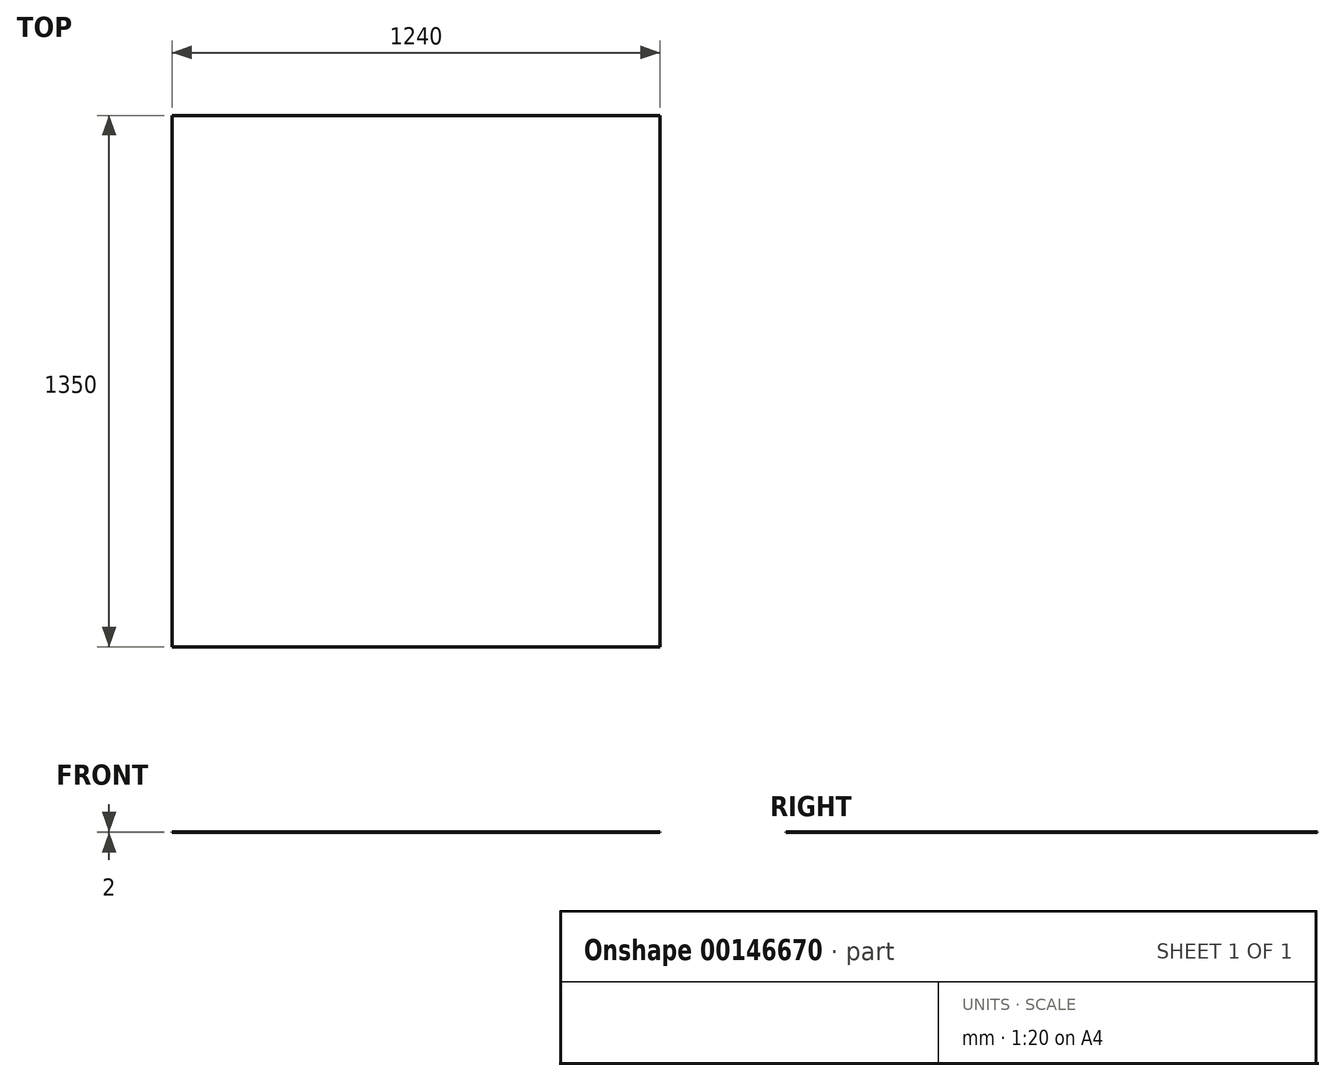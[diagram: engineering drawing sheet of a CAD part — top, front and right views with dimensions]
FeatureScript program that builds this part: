
annotation { "Feature Type Name" : "Feature", "Feature Type Description" : "" }
export const myFeature = defineFeature(function(context is Context, id is Id, definition is map)
    precondition{}
    {
        {
            var Q0;
            Q0=qCreatedBy(makeId("Top.planeOp"),FACE);
            var sketch = newSketch(context, id + "F0", { "sketchPlane" : qUnion([Q0])});
            skLineSegment(sketch, "E0.bottom", {"start": v(0, 0) * mm, "end": v(1240, 0) * mm, "construction": true});
            skLineSegment(sketch, "E0.top", {"start": v(0, 1350) * mm, "end": v(1240, 1350) * mm});
            skLineSegment(sketch, "E0.left", {"start": v(0, 0) * mm, "end": v(0, 1350) * mm});
            skLineSegment(sketch, "E0.right", {"start": v(1240, 0) * mm, "end": v(1240, 1350) * mm});
            skLineSegment(sketch, "E1", {"start": v(0, 0) * mm, "end": v(1240, 0) * mm});
            skSolve(sketch);
        }
        {
            var Q0;
            Q0=makeQuery(id+"F0.imprint","IMPRINT",FACE,{"disambiguationData":[TD([[makeQuery(id+"F0.imprint","IMPRINT",EDGE,{"derivedFrom":sQuery(id+"F0.wireOp",EDGE,"E0.top")}),-1.0]])]});
            extrude(context, id + "F1", {"entities" : qUnion([Q0]), "depth" : 2 * mm});
        }
    });
